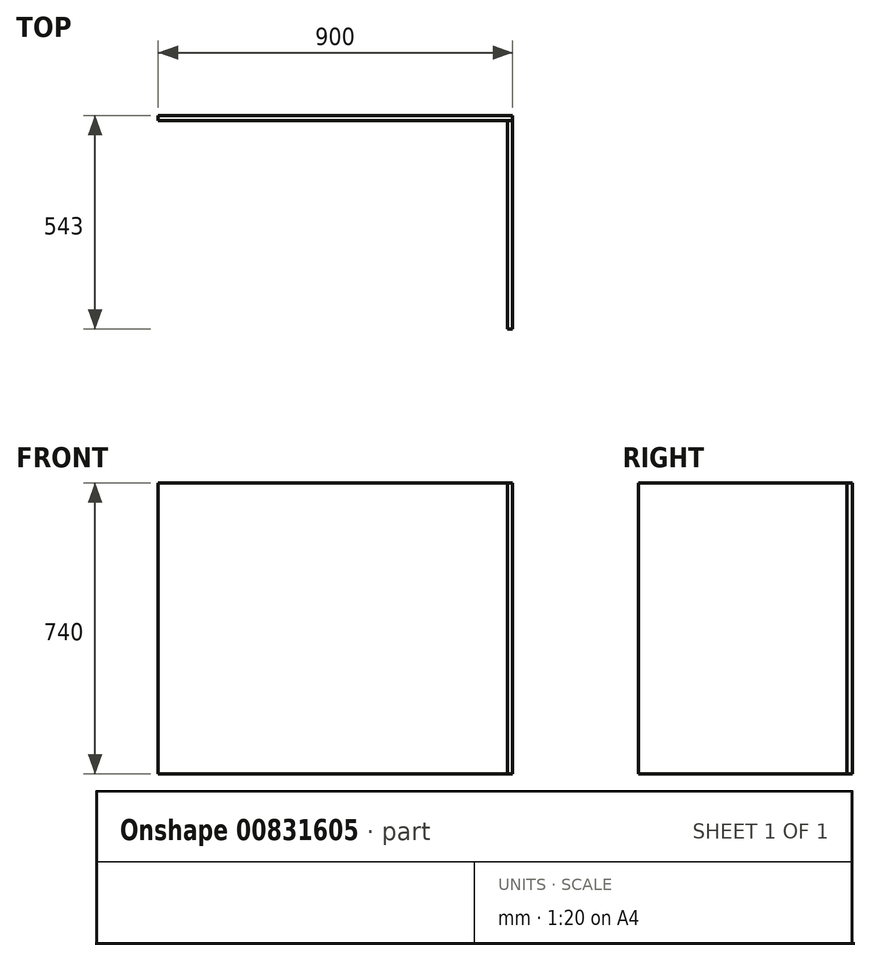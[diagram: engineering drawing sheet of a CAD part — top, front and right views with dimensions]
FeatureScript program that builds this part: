
annotation { "Feature Type Name" : "Feature", "Feature Type Description" : "" }
export const myFeature = defineFeature(function(context is Context, id is Id, definition is map)
    precondition{}
    {
        {
            var Q0;
            Q0=qCreatedBy(makeId("Front.planeOp"),FACE);
            var sketch = newSketch(context, id + "F0", { "sketchPlane" : qUnion([Q0])});
            skLineSegment(sketch, "E0.bottom", {"start": v(450, 370) * mm, "end": v(-450, 370) * mm});
            skLineSegment(sketch, "E0.top", {"start": v(450, -370) * mm, "end": v(-450, -370) * mm});
            skLineSegment(sketch, "E0.left", {"start": v(450, 370) * mm, "end": v(450, -370) * mm});
            skLineSegment(sketch, "E0.right", {"start": v(-450, 370) * mm, "end": v(-450, -370) * mm});
            skPoint(sketch, "E0.middle", {"position": v(0, 0) * mm});
            skSolve(sketch);
        }
        {
            var Q0;
            Q0=makeQuery(id+"F0.imprint","IMPRINT",FACE,{"disambiguationData":[TD([[makeQuery(id+"F0.imprint","IMPRINT",EDGE,{"derivedFrom":sQuery(id+"F0.wireOp",EDGE,"E0.bottom")}),1.0]])]});
            extrude(context, id + "F1", {"entities" : qUnion([Q0]), "depth" : 13 * mm, "offsetDistance" : 25 * mm});
        }
        {
            var Q0;
            Q0=makeQuery(id+"F1.opExtrude","CAP_VERTEX",VERTEX,{"disambiguationData":[OSD([sQuery(id+"F0.wireOp",EDGE,"E0.bottom"),sQuery(id+"F0.wireOp",EDGE,"E0.left")])],"isStart":false});
            var Q1;
            Q1=makeQuery(id+"F1.opExtrude","CAP_VERTEX",VERTEX,{"disambiguationData":[OSD([sQuery(id+"F0.wireOp",EDGE,"E0.top"),sQuery(id+"F0.wireOp",EDGE,"E0.left")])],"isStart":false});
            var Q2;
            Q2=makeQuery(id+"F1.opExtrude","CAP_VERTEX",VERTEX,{"disambiguationData":[OSD([sQuery(id+"F0.wireOp",EDGE,"E0.top"),sQuery(id+"F0.wireOp",EDGE,"E0.left")])],"isStart":true});
            cPlane(context, id + "F2", {"entities" : qUnion([Q0, Q1, Q2]), "cplaneType" : CPlaneType.THREE_POINT, "offset" : 25 * mm, "width" : 150 * mm, "height" : 150 * mm});
        }
        {
            var Q0;
            Q0=qCreatedBy(id+"F2.planeOp",FACE);
            var sketch = newSketch(context, id + "F3", { "sketchPlane" : qUnion([Q0])});
            skLineSegment(sketch, "E1.bottom", {"start": v(13, 370) * mm, "end": v(543, 370) * mm});
            skLineSegment(sketch, "E1.top", {"start": v(13, -370) * mm, "end": v(543, -370) * mm});
            skLineSegment(sketch, "E1.right", {"start": v(543, 370) * mm, "end": v(543, -370) * mm});
            skPoint(sketch, "E2.0", {"position": v(13, -370) * mm});
            skLineSegment(sketch, "E3", {"start": v(13, 370) * mm, "end": v(13, -370) * mm});
            skSolve(sketch);
        }
        {
            var Q0;
            Q0=makeQuery(id+"F3.imprint","IMPRINT",FACE,{"disambiguationData":[TD([[makeQuery(id+"F3.imprint","IMPRINT",EDGE,{"derivedFrom":sQuery(id+"F3.wireOp",EDGE,"E1.bottom")}),-1.0]])]});
            extrude(context, id + "F4", {"entities" : qUnion([Q0]), "depth" : 13 * mm, "offsetDistance" : 25 * mm});
        }
    });
